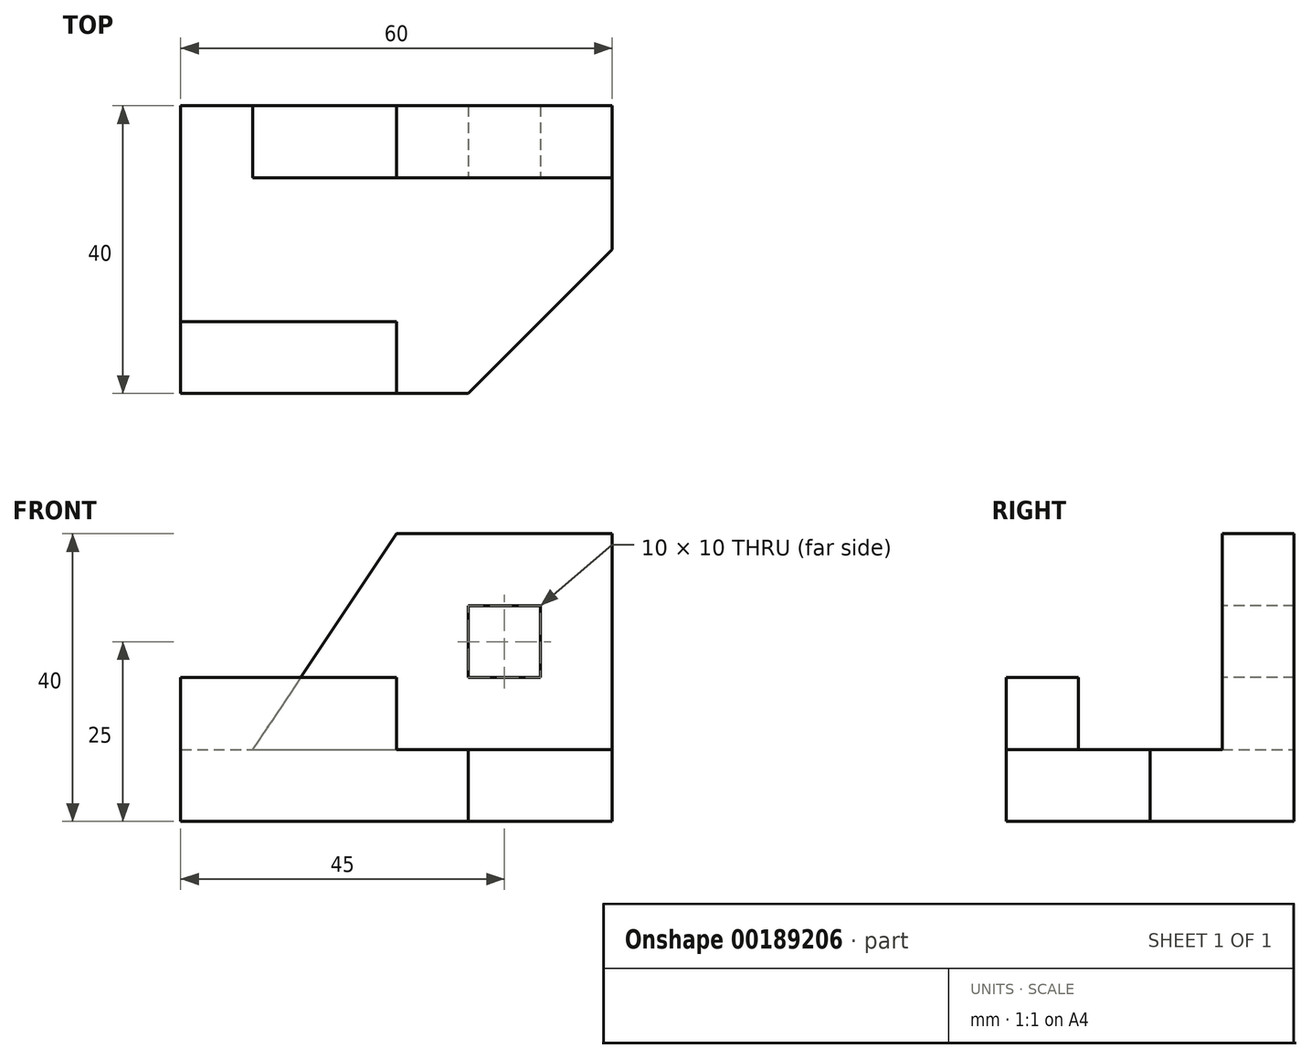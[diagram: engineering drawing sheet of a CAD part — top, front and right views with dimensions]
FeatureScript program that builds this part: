
annotation { "Feature Type Name" : "Feature", "Feature Type Description" : "" }
export const myFeature = defineFeature(function(context is Context, id is Id, definition is map)
    precondition{}
    {
        {
            var Q0;
            Q0=qCreatedBy(makeId("Top.planeOp"),FACE);
            var sketch = newSketch(context, id + "F0", { "sketchPlane" : qUnion([Q0])});
            skLineSegment(sketch, "E0.bottom", {"start": v(0, 0) * mm, "end": v(40, 0) * mm});
            skLineSegment(sketch, "E0.top", {"start": v(0, 40) * mm, "end": v(60, 40) * mm});
            skLineSegment(sketch, "E0.left", {"start": v(0, 0) * mm, "end": v(0, 40) * mm});
            skLineSegment(sketch, "E0.right", {"start": v(60, 20) * mm, "end": v(60, 40) * mm});
            skLineSegment(sketch, "E1", {"start": v(40, 0) * mm, "end": v(60, 20) * mm});
            skSolve(sketch);
        }
        {
            var Q0;
            Q0=makeQuery(id+"F0.imprint","IMPRINT",FACE,{"disambiguationData":[TD([[makeQuery(id+"F0.imprint","IMPRINT",EDGE,{"derivedFrom":sQuery(id+"F0.wireOp",EDGE,"E0.bottom")}),1.0]])]});
            extrude(context, id + "F1", {"entities" : qUnion([Q0]), "depth" : 10 * mm});
        }
        {
            var Q0;
            Q0=makeQuery(id+"F1.opExtrude","SWEPT_FACE",FACE,{"disambiguationData":[OSD([sQuery(id+"F0.wireOp",EDGE,"E0.bottom")])]});
            var sketch = newSketch(context, id + "F2", { "sketchPlane" : qUnion([Q0])});
            skLineSegment(sketch, "E2.bottom", {"start": v(0, 10) * mm, "end": v(30, 10) * mm});
            skLineSegment(sketch, "E2.top", {"start": v(0, 20) * mm, "end": v(30, 20) * mm});
            skLineSegment(sketch, "E2.left", {"start": v(0, 10) * mm, "end": v(0, 20) * mm});
            skLineSegment(sketch, "E2.right", {"start": v(30, 10) * mm, "end": v(30, 20) * mm});
            skSolve(sketch);
        }
        {
            var Q0;
            Q0=makeQuery(id+"F2.imprint","IMPRINT",FACE,{"disambiguationData":[TD([[makeQuery(id+"F2.imprint","IMPRINT",EDGE,{"derivedFrom":sQuery(id+"F2.wireOp",EDGE,"E2.bottom")}),1.0]])]});
            extrude(context, id + "F3", {"entities" : qUnion([Q0]), "operationType" : NewBodyOperationType.ADD, "oppositeDirection" : true, "depth" : 10 * mm});
        }
        {
            var Q0;
            Q0=makeQuery(id+"F1.opExtrude","SWEPT_FACE",FACE,{"disambiguationData":[OSD([sQuery(id+"F0.wireOp",EDGE,"E0.top")])]});
            var sketch = newSketch(context, id + "F4", { "sketchPlane" : qUnion([Q0])});
            skLineSegment(sketch, "E3", {"start": v(-60, 10) * mm, "end": v(-60, 40) * mm});
            skLineSegment(sketch, "E4", {"start": v(-60, 40) * mm, "end": v(-30, 40) * mm});
            skLineSegment(sketch, "E5", {"start": v(-30, 40) * mm, "end": v(-10, 10) * mm});
            skLineSegment(sketch, "E6.0", {"start": v(-10, 10) * mm, "end": v(-60, 10) * mm});
            skPoint(sketch, "E7.orphan", {"position": v(0, 10) * mm});
            skSolve(sketch);
        }
        {
            var Q0;
            Q0=makeQuery(id+"F4.imprint","IMPRINT",FACE,{"disambiguationData":[TD([[makeQuery(id+"F4.imprint","IMPRINT",EDGE,{"derivedFrom":sQuery(id+"F4.wireOp",EDGE,"E3")}),-1.0]])]});
            extrude(context, id + "F5", {"entities" : qUnion([Q0]), "operationType" : NewBodyOperationType.ADD, "oppositeDirection" : true, "depth" : 10 * mm});
        }
        {
            var Q0;
            Q0=makeQuery(id+"F5.opExtrude","CAP_FACE",FACE,{"disambiguationData":[OSD([sQuery(id+"F4.wireOp",EDGE,"E3"),sQuery(id+"F4.wireOp",EDGE,"E4"),sQuery(id+"F4.wireOp",EDGE,"E5"),sQuery(id+"F4.wireOp",EDGE,"E6.0")])],"isStart":false});
            var sketch = newSketch(context, id + "F6", { "sketchPlane" : qUnion([Q0])});
            skLineSegment(sketch, "E8.bottom", {"start": v(40, 30) * mm, "end": v(50, 30) * mm});
            skLineSegment(sketch, "E8.top", {"start": v(40, 20) * mm, "end": v(50, 20) * mm});
            skLineSegment(sketch, "E8.left", {"start": v(40, 30) * mm, "end": v(40, 20) * mm});
            skLineSegment(sketch, "E8.right", {"start": v(50, 30) * mm, "end": v(50, 20) * mm});
            skSolve(sketch);
        }
        {
            var Q0;
            Q0=makeQuery(id+"F6.imprint","IMPRINT",FACE,{"disambiguationData":[TD([[makeQuery(id+"F6.imprint","IMPRINT",EDGE,{"derivedFrom":sQuery(id+"F6.wireOp",EDGE,"E8.bottom")}),-1.0]])]});
            extrude(context, id + "F7", {"entities" : qUnion([Q0]), "operationType" : NewBodyOperationType.REMOVE, "endBound" : BoundingType.THROUGH_ALL, "oppositeDirection" : true, "depth" : 25 * mm});
        }
    });
